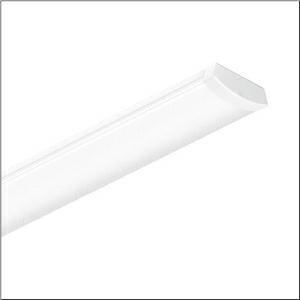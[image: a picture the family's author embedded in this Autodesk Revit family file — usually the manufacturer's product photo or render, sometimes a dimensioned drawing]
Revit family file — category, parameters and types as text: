
# Revit family: siluette_21_51ln12mnm70a
name_source: partatom
category: Lighting Fixtures
units: mm (PartAtom-declared; Revit-internal decimal feet)

## family parameters
Cut with Voids When Loaded = No
Host = Face
Light Source = No
Part Type = Normal
Room Calculation Point = No
Round Connector Dimension = Use Diameter
Shared = No

## types (1)
- --- (1 x LED, 4320 lm, 28.8 W, 5000K)
    Apparent Load = 29 VA
    CIE Flux Codes = 43 73 92 94 100
    Color Rendering = 80
    Color Temperature = 5000K
    Default Elevation = 1800 mm
    Description = Siluette 21, office luminaire, primary optical cover: enclosure, of PC, frosted, light emission: direct distribution, primary light characteristic: symmetric, installation type: suspended mounting, surface-mounted, LED, rated luminous flux: 7.150lm, luminous efficacy: 147lm/W, light colour: 830/840/850, colour temperature: 3000/4000/5000K, control gear: ON/OFF Multilumen, with terminal, 3-pole, mains connection: 220..240V, AC, 50/60Hz, rated input power: 49W, housing, of sheet steel, white, length: 1.500mm, width: 152mm, height: 53mm, end cap, of PMMA, white, protection rating (complete): IP44, insulation class (complete): insulation class I (protective earthing), certification: CE, UKCA, protection symbol: D, impact resistance: IK04, permissible operating ambient temperature: -20..+40°C, contact your sales advisor before using the luminaires in applications with unclear chemical exposure, large temperature fluctuations or condensation-forming humidity, corresponds to IFS (International Featured Standards) requirements for safety and quality in the food industry, packaging unit: 1 piece
    Height = 52 mm  [stored 0.170604 ft]
    Lamp = 1 x LED
    Lamp Light Flux = 4320 lm
    Lamp Power = 28.8 W
    Lamp count = 1
    Length = 1485 mm
    Luminous efficacy = 150 lm/W
    Manufacturer = Siteco
    ModVariant = No
    Model = 51LN12MNM70A
    Mounting Place = Ceiling
    Mounting Type = Pendant
    Number of Poles = 1
    OnlyDefault = Yes
    Power Factor = 1
    Product Name = Siluette 21
    Product group = office luminaire | ceiling pendant
    ProductGroupID = 903
    Protection Class = Protection class I
    Protection Degree = IP 44
    RLX_Detail_Level = 1
    RLX_Emergency_Light_Flux = 0 lm
    RLX_Emergency_Type = 0
    RLX_Emergency_Type_DB = No
    RlxData = <blob elided: 19177 chars, md5=dc36cfc2>
    Socket = socket
    Standby Power = 0 W
    System Light Flux = 4320 lm
    System Power = 29 W
    Type Comments = individual setting: colour temperature 5000K, luminous flux: 61 % | (OFF | OFF | ON) | 200 mA
    Type Image = l_1296910.jpg
    URL = http://relux.com
    VarID = @adj_065797
    Voltage = 0 V
    Weight = 0.00 kg
    Width = 152 mm

note: [stored X ft] marks values corroborated as IEEE doubles in the binary element streams (Revit-internal decimal feet)

## geometry (parser evidence)
native form markers: Blend x4, Sweep x12
no freeform markers — native parametric forms only
